# Revit family: Faucet-Wall_Mount-Lavatory-KOHLER-Singulier-K-10863IN_1
name_source: partatom
category: Plumbing Fixtures
revit_build: Autodesk Revit 2017 (Build: 20160225_1515(x64)
units: mm (PartAtom-declared; Revit-internal decimal feet)

## family parameters
Cut with Voids When Loaded = No
Host = Face
OmniClass Number = 23.31.11.00
OmniClass Title = Faucets
Part Type = Normal
Room Calculation Point = No
Round Connector Dimension = Use Diameter
Shared = No

## types (3) — shared parameters
ADA Compliant = No
Assembly Code = D2010
CW Connection = Yes
Cold Water Inlet = Cold Water Inlet
Date Modified = 09/11/2020
Default Elevation = 36"
Drain Included = No
Flow Rate = 2 GPM
HW Connection = Yes
Handle Clearance = 3 3/8"
Height = 3 1/8"
Hot Water Inlet = Hot Water Inlet
Length = 6 5/8"
Manufacturer = KOHLER Co.
Master Format 2014 = 22 41 39
Master Format 2014 Name = Residential Faucets, Supplies, and Trim
Material = Premium Metal Construction
Pressure = 45.00 psi
Product Name = Singulier
Spout Reach = 6 5/8"
URL = https://www.kohler.co.in
Vent Connection = No
Waste Connection = No
Waste Water Outlet = Waste Water Outlet
WaterSense Certified = No
Width = 4"

## per-type parameters (varying)
| type | Description | Finish | Model | Type |
| CP-Polished Chrome | Wall Mount Single Control LAV Faucet | Kohler-Metal-CP-Polished_Chrome | K-10863IN-4ND-CP | 1 |
| AF-Vibrant French Gold | Wall Mount Single Control LAV W/O Drain | Kohler-Metal-AF-Vibrant_French_Gold | K-10863IN-4ND-AF | 2 |
| PGD-Modern Polished Gold | Wall Mount Single Control LAV Faucet | Kohler-Metal-PGD-Modern_Polished_Gold | K-10863IN-4ND-PGD | 3 |

## geometry (parser evidence)
native form markers: Sweep x5
no freeform markers — native parametric forms only
